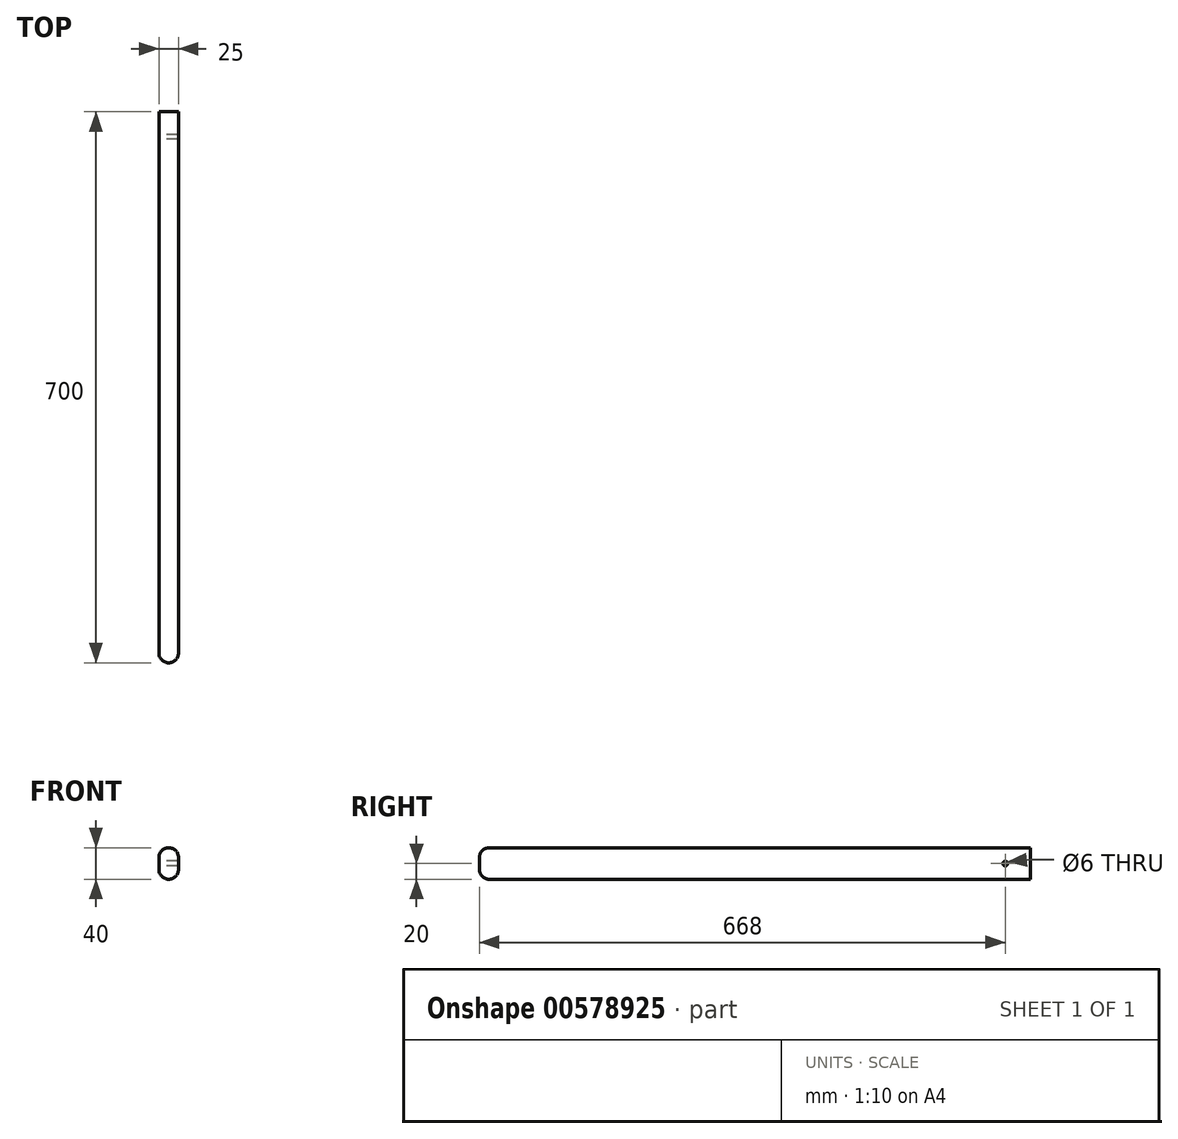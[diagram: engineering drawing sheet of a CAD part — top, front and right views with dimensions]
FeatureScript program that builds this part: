
annotation { "Feature Type Name" : "Feature", "Feature Type Description" : "" }
export const myFeature = defineFeature(function(context is Context, id is Id, definition is map)
    precondition{}
    {
        {
            var Q0;
            Q0=qCreatedBy(makeId("Front.planeOp"),FACE);
            var sketch = newSketch(context, id + "F0", { "sketchPlane" : qUnion([Q0])});
            skLineSegment(sketch, "E0.bottom", {"start": v(0, 20) * mm, "end": v(0, 20) * mm});
            skLineSegment(sketch, "E0.top", {"start": v(0, -20) * mm, "end": v(0, -20) * mm});
            skLineSegment(sketch, "E0.left", {"start": v(12.5, 7.5) * mm, "end": v(12.5, -7.5) * mm});
            skLineSegment(sketch, "E0.right", {"start": v(-12.5, 7.5) * mm, "end": v(-12.5, -7.5) * mm});
            skPoint(sketch, "E0.middle", {"position": v(0, 0) * mm});
            skPoint(sketch, "E1.visualSharp", {"position": v(-12.5, 20) * mm});
            skArc(sketch, "E1.filletArc", {"start": v(0, 20) * mm, "mid": v(-8.84, 16.34) * mm, "end": v(-12.5, 7.5) * mm});
            skPoint(sketch, "E2.visualSharp", {"position": v(12.5, 20) * mm});
            skArc(sketch, "E2.filletArc", {"start": v(12.5, 7.5) * mm, "mid": v(8.84, 16.34) * mm, "end": v(0, 20) * mm});
            skPoint(sketch, "E3.visualSharp", {"position": v(12.5, -20) * mm});
            skArc(sketch, "E3.filletArc", {"start": v(0, -20) * mm, "mid": v(8.84, -16.34) * mm, "end": v(12.5, -7.5) * mm});
            skPoint(sketch, "E4.visualSharp", {"position": v(-12.5, -20) * mm});
            skArc(sketch, "E4.filletArc", {"start": v(-12.5, -7.5) * mm, "mid": v(-8.84, -16.34) * mm, "end": v(0, -20) * mm});
            skSolve(sketch);
        }
        {
            var Q0;
            Q0 = qSketchRegion(id + "F0", true);
            extrude(context, id + "F1", {"entities" : qUnion([Q0]), "depth" : 700 * mm, "offsetDistance" : 25 * mm});
        }
        {
            var Q0;
            Q0=makeQuery(id+"F1.opExtrude","CAP_EDGE",EDGE,{"disambiguationData":[OSD([sQuery(id+"F0.wireOp",EDGE,"E3.filletArc"),sQuery(id+"F0.wireOp",EDGE,"E4.filletArc")])],"isStart":false});
            fillet(context, id + "F2", {"entities" : qUnion([Q0]), "radius" : 12.5 * mm, "tangentPropagation" : true, "allowEdgeOverflow" : false});
        }
        {
            var Q0;
            Q0=makeQuery(id+"F1.opExtrude","SWEPT_FACE",FACE,{"disambiguationData":[OSD([sQuery(id+"F0.wireOp",EDGE,"E0.right")])]});
            var sketch = newSketch(context, id + "F3", { "sketchPlane" : qUnion([Q0])});
            skCircle(sketch, "E5", {"center": v(32, 0) * mm, "radius": 3 * mm});
            skSolve(sketch);
        }
        {
            var Q0;
            Q0=makeQuery(id+"F3.imprint","IMPRINT",FACE,{"disambiguationData":[TD([[makeQuery(id+"F3.imprint","IMPRINT",EDGE,{"derivedFrom":sQuery(id+"F3.wireOp",EDGE,"E5")}),1.0]])]});
            extrude(context, id + "F4", {"entities" : qUnion([Q0]), "operationType" : NewBodyOperationType.REMOVE, "endBound" : BoundingType.THROUGH_ALL, "oppositeDirection" : true, "depth" : 25 * mm, "offsetDistance" : 25 * mm});
        }
    });
